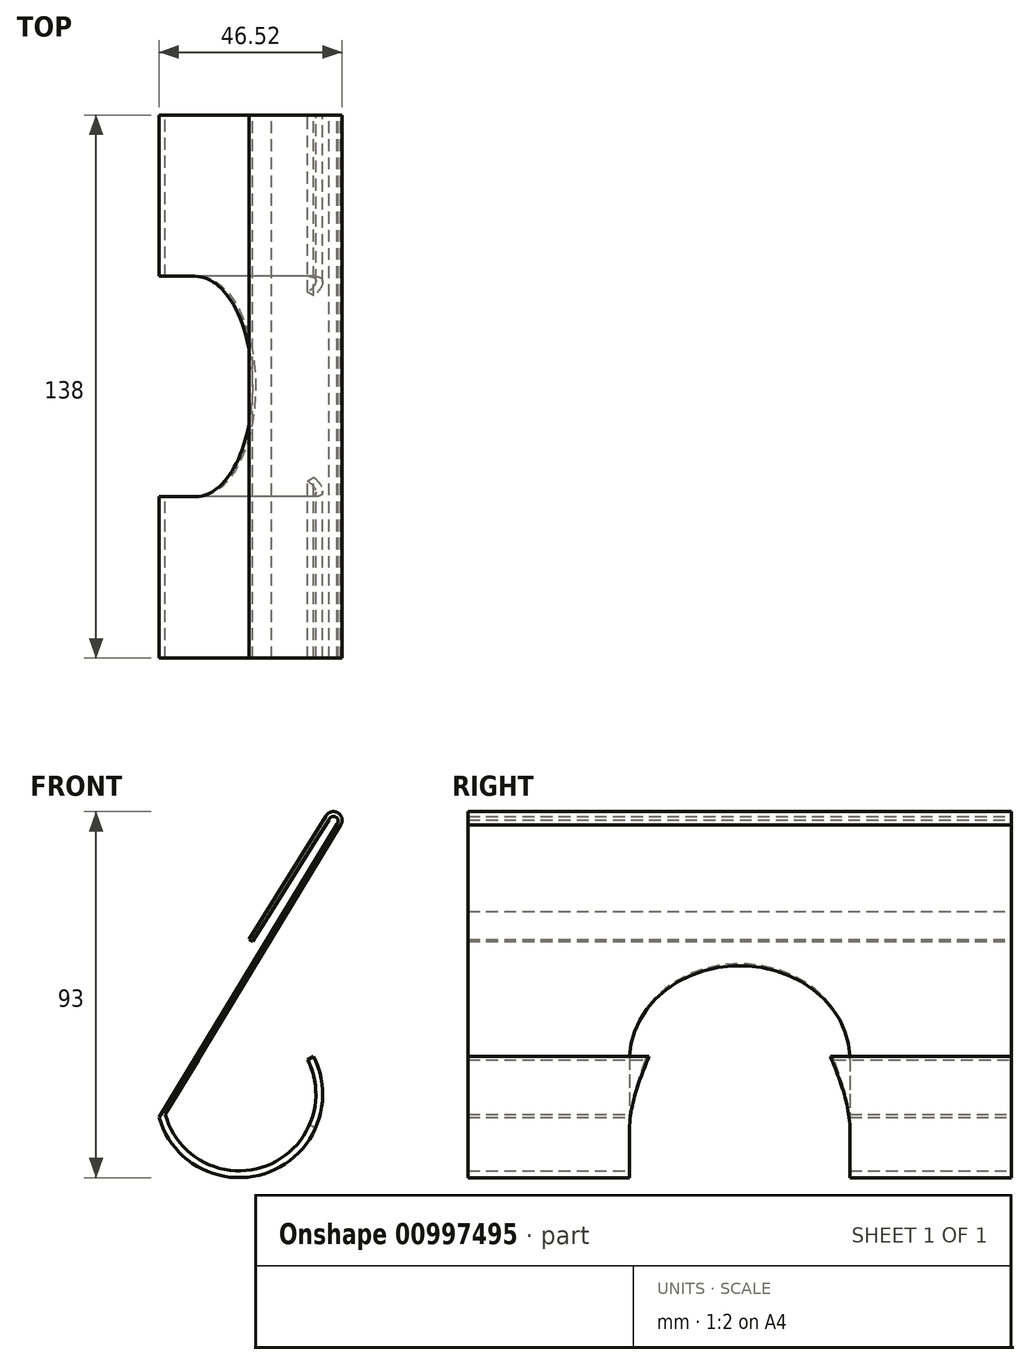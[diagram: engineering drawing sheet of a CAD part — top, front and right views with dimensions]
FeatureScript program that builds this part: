
annotation { "Feature Type Name" : "Feature", "Feature Type Description" : "" }
export const myFeature = defineFeature(function(context is Context, id is Id, definition is map)
    precondition{}
    {
        {
            var Q0;
            Q0=qCreatedBy(makeId("Front.planeOp"),FACE);
            var sketch = newSketch(context, id + "F0", { "sketchPlane" : qUnion([Q0])});
            skLineSegment(sketch, "E0", {"start": v(-105.68, -106.66) * mm, "end": v(-105.68, -106.66) * mm});
            skLineSegment(sketch, "E1", {"start": v(-100.37, -95.82) * mm, "end": v(-103.73, -101.21) * mm});
            skLineSegment(sketch, "E2", {"start": v(-108.59, -108.95) * mm, "end": v(-108.5, -108.95) * mm});
            skPoint(sketch, "E2.endSnap0", {"position": v(-107.14, -107.84) * mm});
            skLineSegment(sketch, "E3", {"start": v(-101.9, -101.67) * mm, "end": v(-101.93, -101.72) * mm});
            skLineSegment(sketch, "E4", {"start": v(-102, -101.7) * mm, "end": v(-101.9, -101.67) * mm});
            skLineSegment(sketch, "E5", {"start": v(-102, -101.7) * mm, "end": v(-101.93, -101.72) * mm});
            skLineSegment(sketch, "E6", {"start": v(-115.85, -118.45) * mm, "end": v(-101.1, -94.78) * mm});
            skArc(sketch, "E7", {"start": v(-97.34, -97.18) * mm, "mid": v(-98, -94.08) * mm, "end": v(-101.1, -94.78) * mm});
            skArc(sketch, "E8", {"start": v(-98.22, -96.87) * mm, "mid": v(-98.68, -95.07) * mm, "end": v(-100.37, -95.82) * mm});
            skLineSegment(sketch, "E9", {"start": v(-98.22, -96.87) * mm, "end": v(-132.66, -153.59) * mm});
            skLineSegment(sketch, "E10", {"start": v(-97.34, -97.18) * mm, "end": v(-141.92, -170.6) * mm});
            skLineSegment(sketch, "E11", {"start": v(-132.66, -153.59) * mm, "end": v(-143.5, -171.43) * mm});
            skArc(sketch, "E12", {"start": v(-143.5, -171.43) * mm, "mid": v(-115.37, -185.25) * mm, "end": v(-104.2, -155.97) * mm});
            skLineSegment(sketch, "E13.trimOffspring", {"start": v(-108.55, -108.95) * mm, "end": v(-108.59, -109.01) * mm});
            skPoint(sketch, "E14.endSnap0", {"position": v(-112.17, -115.88) * mm});
            skLineSegment(sketch, "E15", {"start": v(-103.73, -101.21) * mm, "end": v(-114.88, -119.05) * mm});
            skPoint(sketch, "E16.end.orphan", {"position": v(-113.43, -117.73) * mm});
            skPoint(sketch, "E14.end.orphan", {"position": v(-112.17, -116.52) * mm});
            skPoint(sketch, "E17.orphan", {"position": v(-113.43, -116.75) * mm});
            skPoint(sketch, "E18.end.orphan", {"position": v(-110.92, -115.01) * mm});
            skPoint(sketch, "E19.orphan", {"position": v(-107.14, -108.95) * mm});
            skLineSegment(sketch, "E20.trimOffspring", {"start": v(-108.5, -108.95) * mm, "end": v(-108.59, -109.01) * mm});
            skLineSegment(sketch, "E21", {"start": v(-115.85, -118.45) * mm, "end": v(-127.38, -136.95) * mm});
            skLineSegment(sketch, "E22", {"start": v(-126.64, -137.42) * mm, "end": v(-114.88, -119.05) * mm});
            skLineSegment(sketch, "E23", {"start": v(-120.66, -126.17) * mm, "end": v(-119.79, -126.71) * mm});
            skArc(sketch, "E24", {"start": v(-141.92, -170.6) * mm, "mid": v(-116.18, -183.7) * mm, "end": v(-105.75, -156.77) * mm});
            skLineSegment(sketch, "E25", {"start": v(-105.75, -156.77) * mm, "end": v(-104.2, -155.97) * mm});
            skSolve(sketch);
        }
        {
            var Q0;
            {var subQ0=sQuery(id+"F0.wireOp",EDGE,"E1");Q0=makeQuery(id+"F0.imprint","IMPRINT",FACE,{"disambiguationData":[TD([[makeQuery(id+"F0.imprint","IMPRINT",EDGE,{"derivedFrom":subQ0}),-1.0]])]});}
            extrude(context, id + "F1", {"entities" : qUnion([Q0]), "depth" : 138 * mm, "offsetDistance" : 25.4 * mm});
        }
        {
            var Q0;
            Q0=makeQuery(id+"F1.opExtrude","SWEPT_FACE",FACE,{"disambiguationData":[OSD([sQuery(id+"F0.wireOp",EDGE,"E10")])]});
            var sketch = newSketch(context, id + "F2", { "sketchPlane" : qUnion([Q0])});
            skArc(sketch, "E26", {"start": v(-41, -203.3) * mm, "mid": v(-69.26, -175.3) * mm, "end": v(-97, -203.82) * mm});
            skPoint(sketch, "E27", {"position": v(-69, -133.59) * mm});
            skLineSegment(sketch, "E28", {"start": v(-97, -202.79) * mm, "end": v(-97, -251.15) * mm});
            skPoint(sketch, "E29", {"position": v(-69, -191.92) * mm});
            skLineSegment(sketch, "E30", {"start": v(-97, -251.15) * mm, "end": v(-42.35, -251.15) * mm});
            skLineSegment(sketch, "E31", {"start": v(-41, -203.3) * mm, "end": v(-41, -251.15) * mm});
            skLineSegment(sketch, "E32", {"start": v(-42.35, -251.15) * mm, "end": v(-41, -251.15) * mm});
            skPoint(sketch, "E33.orphan", {"position": v(-69, -250.26) * mm});
            skSolve(sketch);
        }
        {
            var Q0;
            {var subQ0=sQuery(id+"F2.wireOp",EDGE,"E31");var subQ1=sQuery(id+"F2.wireOp",EDGE,"E26");var subQ2=makeQuery(id+"F2.imprint","INTERSECT",VERTEX,{"derivedFrom":[subQ1,subQ0]});Q0=makeQuery(id+"F2.imprint","IMPRINT",FACE,{"disambiguationData":[TD([[makeQuery(id+"F2.imprint","IMPRINT",EDGE,{"disambiguationData":[TD([[subQ2,-1.0]])],"derivedFrom":subQ1}),1.0]])]});}
            extrude(context, id + "F3", {"entities" : qUnion([Q0]), "operationType" : NewBodyOperationType.REMOVE, "depth" : 49.4 * mm, "offsetDistance" : 25 * mm});
        }
        {
            var Q0;
            {var subQ4=sQuery(id+"F2.wireOp",EDGE,"E30");Q0=makeQuery(id+"F2.imprint","IMPRINT",FACE,{"disambiguationData":[TD([[makeQuery(id+"F2.imprint","IMPRINT",EDGE,{"derivedFrom":subQ4}),1.0]])]});}
            extrude(context, id + "F4", {"entities" : qUnion([Q0]), "operationType" : NewBodyOperationType.REMOVE, "depth" : 78.6 * mm, "offsetDistance" : 25 * mm});
        }
        {
            var Q0;
            {var subQ0=sQuery(id+"F2.wireOp",EDGE,"E31");var subQ1=sQuery(id+"F2.wireOp",EDGE,"E26");var subQ2=makeQuery(id+"F2.imprint","INTERSECT",VERTEX,{"derivedFrom":[subQ1,subQ0]});Q0=makeQuery(id+"F2.imprint","IMPRINT",FACE,{"disambiguationData":[TD([[makeQuery(id+"F2.imprint","IMPRINT",EDGE,{"disambiguationData":[TD([[subQ2,-1.0]])],"derivedFrom":subQ1}),1.0]])]});}
            extrude(context, id + "F5", {"entities" : qUnion([Q0]), "operationType" : NewBodyOperationType.REMOVE, "oppositeDirection" : true, "depth" : 25 * mm, "offsetDistance" : 25 * mm});
        }
        {
            var Q0;
            {var subQ4=sQuery(id+"F2.wireOp",EDGE,"E30");Q0=makeQuery(id+"F2.imprint","IMPRINT",FACE,{"disambiguationData":[TD([[makeQuery(id+"F2.imprint","IMPRINT",EDGE,{"derivedFrom":subQ4}),1.0]])]});}
            extrude(context, id + "F6", {"entities" : qUnion([Q0]), "operationType" : NewBodyOperationType.REMOVE, "oppositeDirection" : true, "depth" : 25 * mm, "offsetDistance" : 25 * mm});
        }
    });
